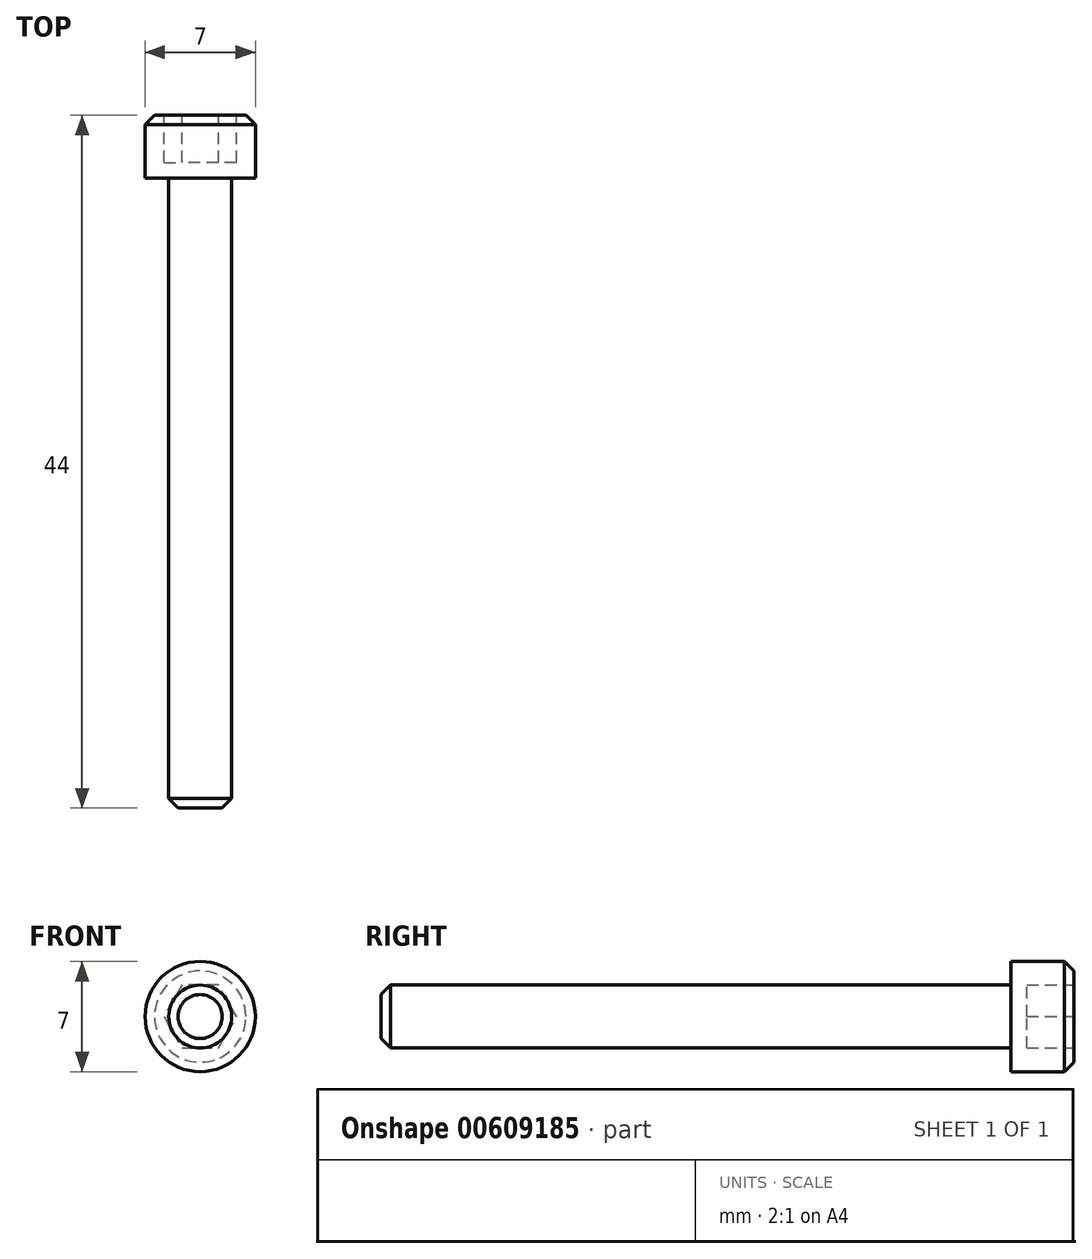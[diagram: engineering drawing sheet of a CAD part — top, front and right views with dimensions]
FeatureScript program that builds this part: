
annotation { "Feature Type Name" : "Feature", "Feature Type Description" : "" }
export const myFeature = defineFeature(function(context is Context, id is Id, definition is map)
    precondition{}
    {
        {
            var Q0;
            Q0=qCreatedBy(makeId("Front.planeOp"),FACE);
            var sketch = newSketch(context, id + "F0", { "sketchPlane" : qUnion([Q0])});
            skCircle(sketch, "E0", {"center": v(0, 0) * mm, "radius": 3.5 * mm});
            skSolve(sketch);
        }
        {
            var Q0;
            Q0=qSketchRegion(id+"F0",true);
            extrude(context, id + "F1", {"entities" : qUnion([Q0]), "depth" : 4 * mm, "offsetDistance" : 25 * mm});
        }
        {
            var Q0;
            Q0=makeQuery(id+"F1.opExtrude","CAP_FACE",FACE,{"disambiguationData":[OSD([sQuery(id+"F0.wireOp",EDGE,"E0")])],"isStart":false});
            var sketch = newSketch(context, id + "F2", { "sketchPlane" : qUnion([Q0])});
            skCircle(sketch, "E1", {"center": v(0, 0) * mm, "radius": 2 * mm});
            skSolve(sketch);
        }
        {
            var Q0;
            Q0=qSketchRegion(id+"F2",true);
            extrude(context, id + "F3", {"entities" : qUnion([Q0]), "operationType" : NewBodyOperationType.ADD, "depth" : 40 * mm, "offsetDistance" : 25 * mm});
        }
        {
            var Q0;
            Q0=makeQuery(id+"F1.opExtrude","CAP_FACE",FACE,{"disambiguationData":[OSD([sQuery(id+"F0.wireOp",EDGE,"E0")])],"isStart":true});
            var sketch = newSketch(context, id + "F4", { "sketchPlane" : qUnion([Q0])});
            skCircle(sketch, "E2.cCircle", {"center": v(0, 0) * mm, "radius": 2 * mm, "construction": true});
            skLineSegment(sketch, "E2.0", {"start": v(-1.15, 2) * mm, "end": v(1.15, 2) * mm});
            skLineSegment(sketch, "E2.1", {"start": v(1.15, 2) * mm, "end": v(2.3, 0) * mm});
            skLineSegment(sketch, "E2.2", {"start": v(2.3, 0) * mm, "end": v(1.15, -2) * mm});
            skLineSegment(sketch, "E2.3", {"start": v(1.15, -2) * mm, "end": v(-1.15, -2) * mm});
            skLineSegment(sketch, "E2.4", {"start": v(-1.15, -2) * mm, "end": v(-2.3, 0) * mm});
            skLineSegment(sketch, "E2.5", {"start": v(-2.3, 0) * mm, "end": v(-1.15, 2) * mm});
            skPoint(sketch, "E2.0.midPoint", {"position": v(0, 2) * mm});
            skSolve(sketch);
        }
        {
            var Q0;
            Q0=qSketchRegion(id+"F4",true);
            extrude(context, id + "F5", {"entities" : qUnion([Q0]), "operationType" : NewBodyOperationType.REMOVE, "oppositeDirection" : true, "depth" : 3 * mm, "offsetDistance" : 25 * mm});
        }
        {
            var Q0;
            Q0=makeQuery(id+"F1.opExtrude","CAP_EDGE",EDGE,{"disambiguationData":[OSD([sQuery(id+"F0.wireOp",EDGE,"E0")])],"isStart":true});
            var Q1;
            Q1=makeQuery(id+"F3.opExtrude","CAP_EDGE",EDGE,{"disambiguationData":[OSD([sQuery(id+"F2.wireOp",EDGE,"E1")])],"isStart":false});
            chamfer(context, id + "F6", {"entities" : qUnion([Q0, Q1]), "width" : 0.6 * mm, "tangentPropagation" : true});
        }
    });
